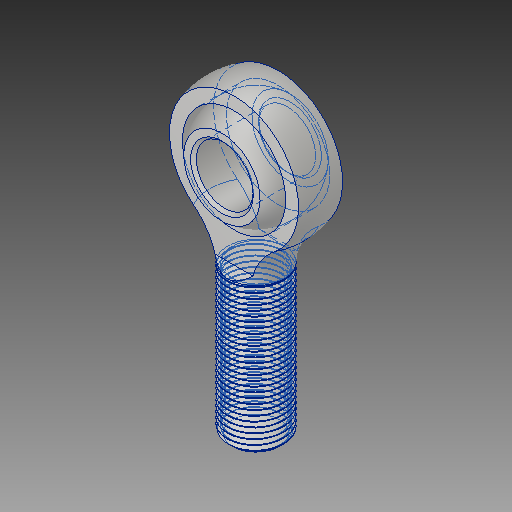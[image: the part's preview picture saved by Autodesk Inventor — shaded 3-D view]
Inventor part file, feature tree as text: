
AUTODESK INVENTOR PART (.ipt)
format: ipt  version: 2019 (Build 230136000, 136)  size: 699,392 bytes
history: native  units: in
note: dims shown in document units (in); Inventor stores cm internally (conversion verified against a paired STEP export)
features: other x1, chamfer x1
ambient origin geometry x8: Origin, YZ Plane, XZ Plane, XY Plane, X Axis, Y Axis, Z Axis, Center Point
bodies: Solid1 (feature_tree), Solid2 (feature_tree)
feature tree (2):
  other  "Cut-Extrude2"
  chamfer  "Chamfer1"  [1 undecoded]
note: 1 required parameter value undecoded (feature->parameter linkage not recoverable at this tier; creation-order binding heuristic only, values carry confidence <= 0.55)
